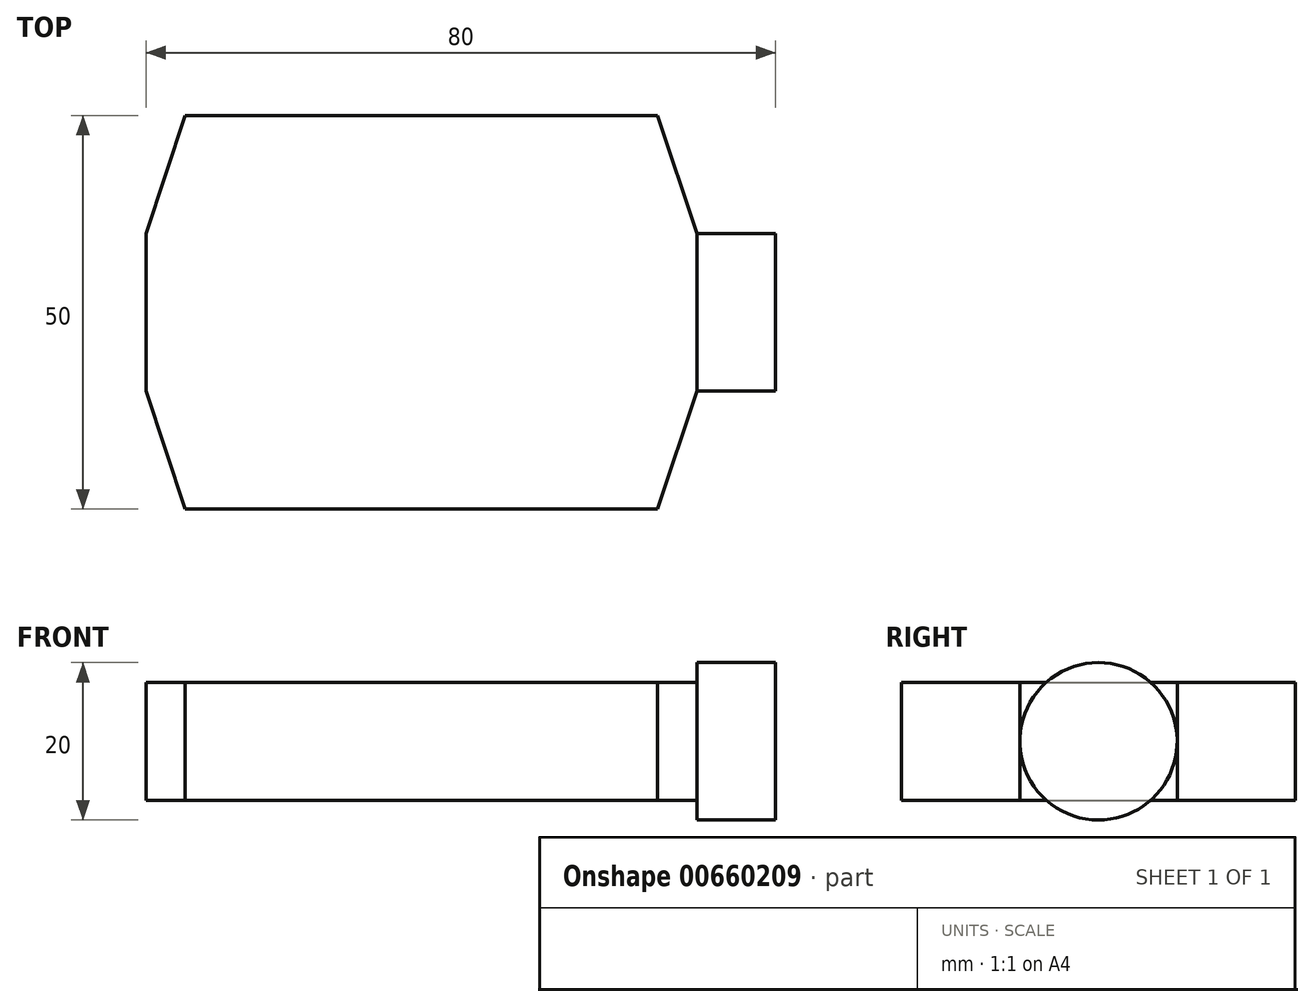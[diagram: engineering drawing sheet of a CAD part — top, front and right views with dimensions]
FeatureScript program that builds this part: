
annotation { "Feature Type Name" : "Feature", "Feature Type Description" : "" }
export const myFeature = defineFeature(function(context is Context, id is Id, definition is map)
    precondition{}
    {
        {
            var Q0;
            Q0=qCreatedBy(makeId("Right.planeOp"),FACE);
            var sketch = newSketch(context, id + "F0", { "sketchPlane" : qUnion([Q0])});
            skCircle(sketch, "E0", {"center": v(0, 0) * mm, "radius": 10 * mm});
            skSolve(sketch);
        }
        {
            var Q0;
            Q0 = qSketchRegion(id + "F0", true);
            extrude(context, id + "F1", {"entities" : qUnion([Q0]), "depth" : 10 * mm, "offsetDistance" : 25 * mm});
        }
        {
            var Q0;
            Q0=qCreatedBy(makeId("Top.planeOp"),FACE);
            var sketch = newSketch(context, id + "F2", { "sketchPlane" : qUnion([Q0])});
            skLineSegment(sketch, "E1.bottom", {"start": v(-65, 25) * mm, "end": v(-5, 25) * mm});
            skLineSegment(sketch, "E1.top", {"start": v(-65, -25) * mm, "end": v(-5, -25) * mm});
            skLineSegment(sketch, "E2.left", {"start": v(-70, -10) * mm, "end": v(-70, 10) * mm});
            skLineSegment(sketch, "E2.right", {"start": v(0, -10) * mm, "end": v(0, 10) * mm});
            skLineSegment(sketch, "E3", {"start": v(-5, -25) * mm, "end": v(0, -10) * mm});
            skLineSegment(sketch, "E4", {"start": v(0, 10) * mm, "end": v(-5, 25) * mm});
            skLineSegment(sketch, "E5", {"start": v(-65, -25) * mm, "end": v(-70, -10) * mm});
            skLineSegment(sketch, "E6", {"start": v(-70, 10) * mm, "end": v(-65, 25) * mm});
            skSolve(sketch);
        }
        {
            var Q0;
            Q0 = qSketchRegion(id + "F2", true);
            extrude(context, id + "F3", {"entities" : qUnion([Q0]), "operationType" : NewBodyOperationType.ADD, "endBound" : BoundingType.SYMMETRIC, "depth" : 15 * mm, "offsetDistance" : 25 * mm});
        }
    });
